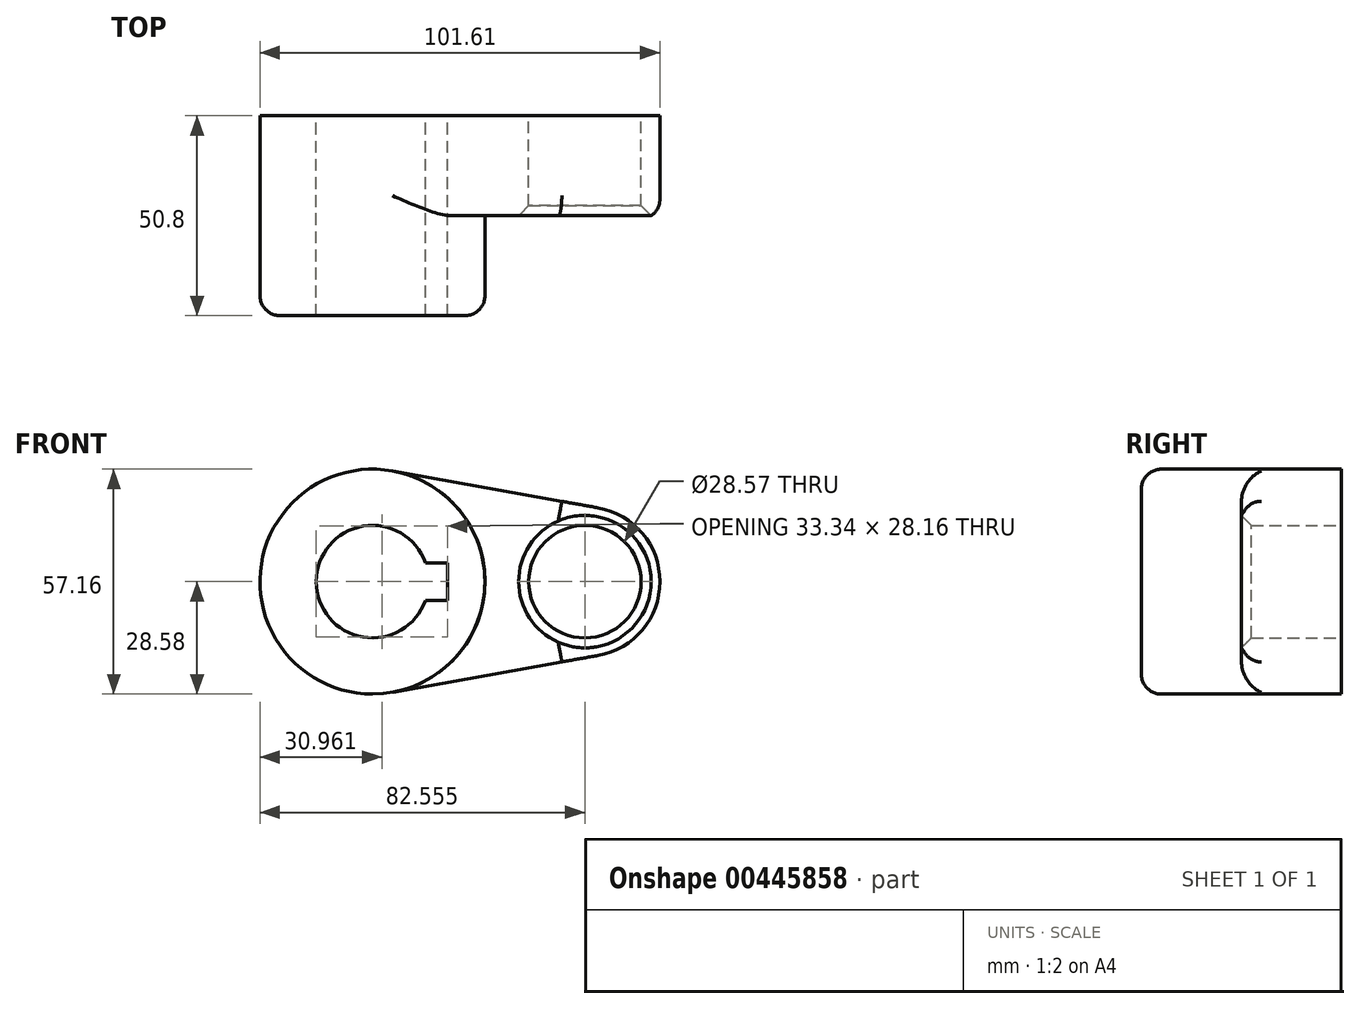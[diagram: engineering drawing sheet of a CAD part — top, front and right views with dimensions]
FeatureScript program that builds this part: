
annotation { "Feature Type Name" : "Feature", "Feature Type Description" : "" }
export const myFeature = defineFeature(function(context is Context, id is Id, definition is map)
    precondition{}
    {
        {
            var Q0;
            Q0=qCreatedBy(makeId("Front.planeOp"),FACE);
            var sketch = newSketch(context, id + "F0", { "sketchPlane" : qUnion([Q0])});
            skCircle(sketch, "E0", {"center": v(0, 0) * mm, "radius": 28.58 * mm});
            skCircle(sketch, "E1", {"center": v(53.98, 0) * mm, "radius": 19.05 * mm});
            skLineSegment(sketch, "E2", {"start": v(5.04, 28.13) * mm, "end": v(57.34, 18.75) * mm});
            skLineSegment(sketch, "E3", {"start": v(5.04, -28.13) * mm, "end": v(57.34, -18.75) * mm});
            skCircle(sketch, "E4", {"center": v(0, 0) * mm, "radius": 14.29 * mm});
            skCircle(sketch, "E5", {"center": v(53.98, 0) * mm, "radius": 14.29 * mm});
            skLineSegment(sketch, "E6.bottom", {"start": v(19.05, 4.76) * mm, "end": v(-19.05, 4.76) * mm});
            skLineSegment(sketch, "E6.top", {"start": v(19.05, -4.76) * mm, "end": v(-19.05, -4.76) * mm});
            skLineSegment(sketch, "E6.left", {"start": v(19.05, 4.76) * mm, "end": v(19.05, -4.76) * mm});
            skLineSegment(sketch, "E6.right", {"start": v(-19.05, 4.76) * mm, "end": v(-19.05, -4.76) * mm});
            skSolve(sketch);
        }
        {
            var Q0;
            {var subQ7=sQuery(id+"F0.wireOp",EDGE,"E6.left");Q0=makeQuery(id+"F0.imprint","IMPRINT",FACE,{"disambiguationData":[TD([[makeQuery(id+"F0.imprint","IMPRINT",EDGE,{"derivedFrom":subQ7}),1.0]])]});}
            var Q1;
            {var subQ0=sQuery(id+"F0.wireOp",EDGE,"E2");Q1=makeQuery(id+"F0.imprint","IMPRINT",FACE,{"disambiguationData":[TD([[makeQuery(id+"F0.imprint","IMPRINT",EDGE,{"derivedFrom":subQ0}),-1.0]])]});}
            var Q2;
            Q2=makeQuery(id+"F0.imprint","IMPRINT",FACE,{"disambiguationData":[TD([[makeQuery(id+"F0.imprint","IMPRINT",EDGE,{"derivedFrom":sQuery(id+"F0.wireOp",EDGE,"E5")}),-1.0]])]});
            var Q3;
            {var subQ5=sQuery(id+"F0.wireOp",EDGE,"E6.right");Q3=makeQuery(id+"F0.imprint","IMPRINT",FACE,{"disambiguationData":[TD([[makeQuery(id+"F0.imprint","IMPRINT",EDGE,{"derivedFrom":subQ5}),1.0]])]});}
            extrude(context, id + "F1", {"entities" : qUnion([Q0, Q1, Q2, Q3]), "depth" : 25.4 * mm});
        }
        {
            var Q0;
            {var subQ7=sQuery(id+"F0.wireOp",EDGE,"E6.left");Q0=makeQuery(id+"F0.imprint","IMPRINT",FACE,{"disambiguationData":[TD([[makeQuery(id+"F0.imprint","IMPRINT",EDGE,{"derivedFrom":subQ7}),1.0]])]});}
            var Q1;
            {var subQ5=sQuery(id+"F0.wireOp",EDGE,"E6.right");Q1=makeQuery(id+"F0.imprint","IMPRINT",FACE,{"disambiguationData":[TD([[makeQuery(id+"F0.imprint","IMPRINT",EDGE,{"derivedFrom":subQ5}),1.0]])]});}
            extrude(context, id + "F2", {"entities" : qUnion([Q0, Q1]), "operationType" : NewBodyOperationType.ADD, "depth" : 50.8 * mm});
        }
        {
            var Q0;
            Q0=makeQuery(id+"F1.opExtrude","CAP_EDGE",EDGE,{"disambiguationData":[OSD([sQuery(id+"F0.wireOp",EDGE,"E5")])],"isStart":false});
            chamfer(context, id + "F3", {"entities" : qUnion([Q0]), "width" : 2.54 * mm, "tangentPropagation" : true});
        }
        {
            var Q0;
            Q0=makeQuery(id+"F1.opExtrude","CAP_EDGE",EDGE,{"disambiguationData":[OSD([sQuery(id+"F0.wireOp",EDGE,"E3")])],"isStart":false});
            var Q1;
            Q1=makeQuery(id+"F2.opExtrude","CAP_EDGE",EDGE,{"disambiguationData":[OSD([sQuery(id+"F0.wireOp",EDGE,"E0")])],"isStart":false});
            fillet(context, id + "F4", {"entities" : qUnion([Q0, Q1]), "radius" : 5.08 * mm, "tangentPropagation" : true, "allowEdgeOverflow" : false});
        }
    });
